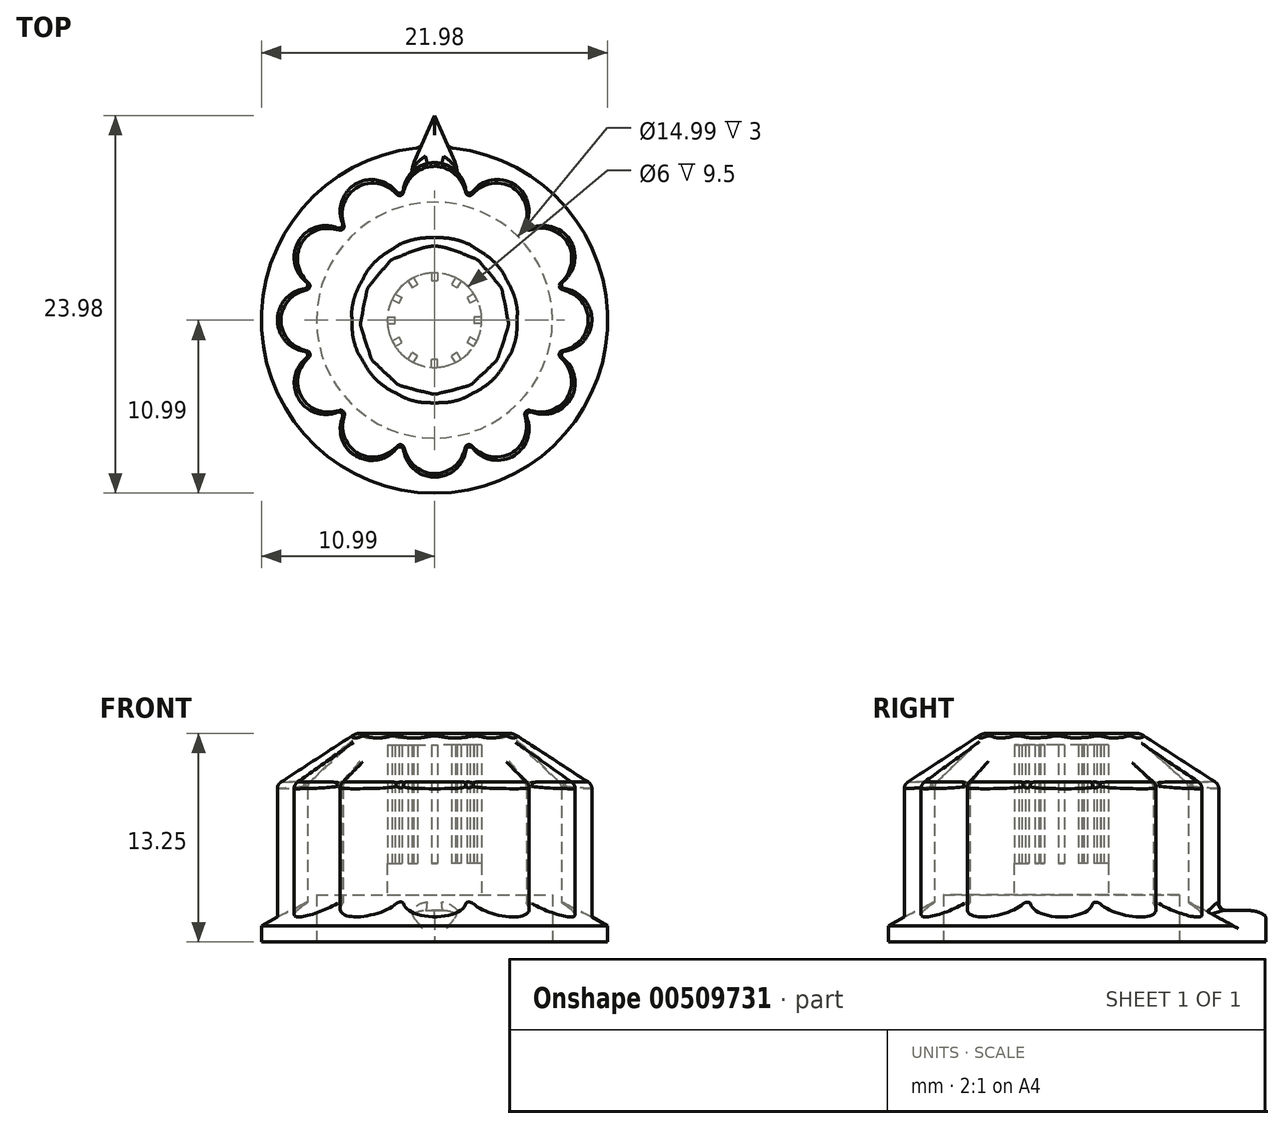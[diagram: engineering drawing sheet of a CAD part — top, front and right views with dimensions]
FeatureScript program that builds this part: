
annotation { "Feature Type Name" : "Feature", "Feature Type Description" : "" }
export const myFeature = defineFeature(function(context is Context, id is Id, definition is map)
    precondition{}
    {
        {
            var Q0;
            Q0=qCreatedBy(makeId("Top.planeOp"),FACE);
            var sketch = newSketch(context, id + "F0", { "sketchPlane" : qUnion([Q0])});
            skArc(sketch, "E0", {"start": v(-1.67, 2.5) * mm, "mid": v(-2.12, 2.12) * mm, "end": v(-2.5, 1.67) * mm});
            skLineSegment(sketch, "E1.top", {"start": v(-0.2, 2.5) * mm, "end": v(0.2, 2.5) * mm});
            skLineSegment(sketch, "E1.left", {"start": v(-0.2, 3) * mm, "end": v(-0.2, 2.5) * mm});
            skLineSegment(sketch, "E1.right", {"start": v(0.2, 3) * mm, "end": v(0.2, 2.5) * mm});
            skLineSegment(sketch, "E2", {"start": v(0, 0) * mm, "end": v(0, 2.5) * mm, "construction": true});
            skLineSegment(sketch, "E3.1.0", {"start": v(-1.32, 2.7) * mm, "end": v(-1.08, 2.27) * mm});
            skLineSegment(sketch, "E3.1.1", {"start": v(-1.42, 2.07) * mm, "end": v(-1.08, 2.27) * mm});
            skLineSegment(sketch, "E3.1.2", {"start": v(-1.67, 2.5) * mm, "end": v(-1.42, 2.07) * mm});
            skLineSegment(sketch, "E3.2.0", {"start": v(-2.5, 1.67) * mm, "end": v(-2.07, 1.42) * mm});
            skLineSegment(sketch, "E3.2.1", {"start": v(-2.27, 1.08) * mm, "end": v(-2.07, 1.42) * mm});
            skLineSegment(sketch, "E3.2.2", {"start": v(-2.7, 1.32) * mm, "end": v(-2.27, 1.08) * mm});
            skLineSegment(sketch, "E3.3.0", {"start": v(-3, 0.2) * mm, "end": v(-2.5, 0.2) * mm});
            skLineSegment(sketch, "E3.3.1", {"start": v(-2.5, -0.2) * mm, "end": v(-2.5, 0.2) * mm});
            skLineSegment(sketch, "E3.3.2", {"start": v(-3, -0.2) * mm, "end": v(-2.5, -0.2) * mm});
            skLineSegment(sketch, "E3.4.0", {"start": v(-2.7, -1.32) * mm, "end": v(-2.27, -1.08) * mm});
            skLineSegment(sketch, "E3.4.1", {"start": v(-2.07, -1.42) * mm, "end": v(-2.27, -1.08) * mm});
            skLineSegment(sketch, "E3.4.2", {"start": v(-2.5, -1.67) * mm, "end": v(-2.07, -1.42) * mm});
            skLineSegment(sketch, "E3.5.0", {"start": v(-1.67, -2.5) * mm, "end": v(-1.42, -2.07) * mm});
            skLineSegment(sketch, "E3.5.1", {"start": v(-1.08, -2.27) * mm, "end": v(-1.42, -2.07) * mm});
            skLineSegment(sketch, "E3.5.2", {"start": v(-1.32, -2.7) * mm, "end": v(-1.08, -2.27) * mm});
            skLineSegment(sketch, "E3.6.0", {"start": v(-0.2, -3) * mm, "end": v(-0.2, -2.5) * mm});
            skLineSegment(sketch, "E3.6.1", {"start": v(0.2, -2.5) * mm, "end": v(-0.2, -2.5) * mm});
            skLineSegment(sketch, "E3.6.2", {"start": v(0.2, -3) * mm, "end": v(0.2, -2.5) * mm});
            skLineSegment(sketch, "E3.7.0", {"start": v(1.32, -2.7) * mm, "end": v(1.08, -2.27) * mm});
            skLineSegment(sketch, "E3.7.1", {"start": v(1.42, -2.07) * mm, "end": v(1.08, -2.27) * mm});
            skLineSegment(sketch, "E3.7.2", {"start": v(1.67, -2.5) * mm, "end": v(1.42, -2.07) * mm});
            skLineSegment(sketch, "E3.8.0", {"start": v(2.5, -1.67) * mm, "end": v(2.07, -1.42) * mm});
            skLineSegment(sketch, "E3.8.1", {"start": v(2.27, -1.08) * mm, "end": v(2.07, -1.42) * mm});
            skLineSegment(sketch, "E3.8.2", {"start": v(2.7, -1.32) * mm, "end": v(2.27, -1.08) * mm});
            skLineSegment(sketch, "E3.9.0", {"start": v(3, -0.2) * mm, "end": v(2.5, -0.2) * mm});
            skLineSegment(sketch, "E3.9.1", {"start": v(2.5, 0.2) * mm, "end": v(2.5, -0.2) * mm});
            skLineSegment(sketch, "E3.9.2", {"start": v(3, 0.2) * mm, "end": v(2.5, 0.2) * mm});
            skLineSegment(sketch, "E3.10.0", {"start": v(2.7, 1.32) * mm, "end": v(2.27, 1.08) * mm});
            skLineSegment(sketch, "E3.10.1", {"start": v(2.07, 1.42) * mm, "end": v(2.27, 1.08) * mm});
            skLineSegment(sketch, "E3.10.2", {"start": v(2.5, 1.67) * mm, "end": v(2.07, 1.42) * mm});
            skLineSegment(sketch, "E3.11.0", {"start": v(1.67, 2.5) * mm, "end": v(1.42, 2.07) * mm});
            skLineSegment(sketch, "E3.11.1", {"start": v(1.08, 2.27) * mm, "end": v(1.42, 2.07) * mm});
            skLineSegment(sketch, "E3.11.2", {"start": v(1.32, 2.7) * mm, "end": v(1.08, 2.27) * mm});
            skArc(sketch, "E4.trimOffspring", {"start": v(-0.2, 3) * mm, "mid": v(-0.78, 2.9) * mm, "end": v(-1.32, 2.7) * mm});
            skArc(sketch, "E5.trimOffspring", {"start": v(1.32, 2.7) * mm, "mid": v(0.78, 2.9) * mm, "end": v(0.2, 3) * mm});
            skArc(sketch, "E6.trimOffspring", {"start": v(2.5, 1.67) * mm, "mid": v(2.12, 2.12) * mm, "end": v(1.67, 2.5) * mm});
            skArc(sketch, "E7.trimOffspring", {"start": v(3, 0.2) * mm, "mid": v(2.9, 0.78) * mm, "end": v(2.7, 1.32) * mm});
            skArc(sketch, "E8.trimOffspring", {"start": v(2.7, -1.32) * mm, "mid": v(2.9, -0.78) * mm, "end": v(3, -0.2) * mm});
            skArc(sketch, "E9.trimOffspring", {"start": v(1.67, -2.5) * mm, "mid": v(2.12, -2.12) * mm, "end": v(2.5, -1.67) * mm});
            skArc(sketch, "E10.trimOffspring", {"start": v(0.2, -3) * mm, "mid": v(0.78, -2.9) * mm, "end": v(1.32, -2.7) * mm});
            skArc(sketch, "E11.trimOffspring", {"start": v(-1.32, -2.7) * mm, "mid": v(-0.78, -2.9) * mm, "end": v(-0.2, -3) * mm});
            skArc(sketch, "E12.trimOffspring", {"start": v(-2.5, -1.67) * mm, "mid": v(-2.12, -2.12) * mm, "end": v(-1.67, -2.5) * mm});
            skArc(sketch, "E13.trimOffspring", {"start": v(-3, -0.2) * mm, "mid": v(-2.9, -0.78) * mm, "end": v(-2.7, -1.32) * mm});
            skArc(sketch, "E14.trimOffspring", {"start": v(-2.7, 1.32) * mm, "mid": v(-2.9, 0.78) * mm, "end": v(-3, 0.2) * mm});
            skCircle(sketch, "E15", {"center": v(0, 0) * mm, "radius": 4 * mm});
            skSolve(sketch);
        }
        {
            var Q0;
            Q0 = qSketchRegion(id + "F0", true);
            extrude(context, id + "F1", {"entities" : qUnion([Q0]), "depth" : 12.25 * mm});
        }
        {
            var Q0;
            Q0=qCreatedBy(makeId("Top.planeOp"),FACE);
            var sketch = newSketch(context, id + "F2", { "sketchPlane" : qUnion([Q0])});
            skCircle(sketch, "E16", {"center": v(0, 0) * mm, "radius": 4 * mm});
            skSolve(sketch);
        }
        {
            var Q0;
            Q0 = qSketchRegion(id + "F2", true);
            extrude(context, id + "F3", {"entities" : qUnion([Q0]), "operationType" : NewBodyOperationType.REMOVE, "depth" : 5 * mm});
        }
        {
            var Q0;
            Q0=makeQuery(id+"F1.opExtrude","CAP_FACE",FACE,{"disambiguationData":[OSD([sQuery(id+"F0.wireOp",EDGE,"E0"),sQuery(id+"F0.wireOp",EDGE,"E1.top"),sQuery(id+"F0.wireOp",EDGE,"E1.left"),sQuery(id+"F0.wireOp",EDGE,"E1.right"),sQuery(id+"F0.wireOp",EDGE,"E3.1.0"),sQuery(id+"F0.wireOp",EDGE,"E3.1.1"),sQuery(id+"F0.wireOp",EDGE,"E3.1.2"),sQuery(id+"F0.wireOp",EDGE,"E3.2.0"),sQuery(id+"F0.wireOp",EDGE,"E3.2.1"),sQuery(id+"F0.wireOp",EDGE,"E3.2.2"),sQuery(id+"F0.wireOp",EDGE,"E3.3.0"),sQuery(id+"F0.wireOp",EDGE,"E3.3.1"),sQuery(id+"F0.wireOp",EDGE,"E3.3.2"),sQuery(id+"F0.wireOp",EDGE,"E3.4.0"),sQuery(id+"F0.wireOp",EDGE,"E3.4.1"),sQuery(id+"F0.wireOp",EDGE,"E3.4.2"),sQuery(id+"F0.wireOp",EDGE,"E3.5.0"),sQuery(id+"F0.wireOp",EDGE,"E3.5.1"),sQuery(id+"F0.wireOp",EDGE,"E3.5.2"),sQuery(id+"F0.wireOp",EDGE,"E3.6.0"),sQuery(id+"F0.wireOp",EDGE,"E3.6.1"),sQuery(id+"F0.wireOp",EDGE,"E3.6.2"),sQuery(id+"F0.wireOp",EDGE,"E3.7.0"),sQuery(id+"F0.wireOp",EDGE,"E3.7.1"),sQuery(id+"F0.wireOp",EDGE,"E3.7.2"),sQuery(id+"F0.wireOp",EDGE,"E3.8.0"),sQuery(id+"F0.wireOp",EDGE,"E3.8.1"),sQuery(id+"F0.wireOp",EDGE,"E3.8.2"),sQuery(id+"F0.wireOp",EDGE,"E3.9.0"),sQuery(id+"F0.wireOp",EDGE,"E3.9.1"),sQuery(id+"F0.wireOp",EDGE,"E3.9.2"),sQuery(id+"F0.wireOp",EDGE,"E3.10.0"),sQuery(id+"F0.wireOp",EDGE,"E3.10.1"),sQuery(id+"F0.wireOp",EDGE,"E3.10.2"),sQuery(id+"F0.wireOp",EDGE,"E3.11.0"),sQuery(id+"F0.wireOp",EDGE,"E3.11.1"),sQuery(id+"F0.wireOp",EDGE,"E3.11.2"),sQuery(id+"F0.wireOp",EDGE,"E4.trimOffspring"),sQuery(id+"F0.wireOp",EDGE,"E5.trimOffspring"),sQuery(id+"F0.wireOp",EDGE,"E6.trimOffspring"),sQuery(id+"F0.wireOp",EDGE,"E7.trimOffspring"),sQuery(id+"F0.wireOp",EDGE,"E8.trimOffspring"),sQuery(id+"F0.wireOp",EDGE,"E9.trimOffspring"),sQuery(id+"F0.wireOp",EDGE,"E10.trimOffspring"),sQuery(id+"F0.wireOp",EDGE,"E11.trimOffspring"),sQuery(id+"F0.wireOp",EDGE,"E12.trimOffspring"),sQuery(id+"F0.wireOp",EDGE,"E13.trimOffspring"),sQuery(id+"F0.wireOp",EDGE,"E14.trimOffspring"),sQuery(id+"F0.wireOp",EDGE,"E15")])],"isStart":false});
            var sketch = newSketch(context, id + "F4", { "sketchPlane" : qUnion([Q0])});
            skCircle(sketch, "E17", {"center": v(0, 0) * mm, "radius": 4 * mm});
            skSolve(sketch);
        }
        {
            var Q0;
            Q0 = qSketchRegion(id + "F4", true);
            extrude(context, id + "F5", {"entities" : qUnion([Q0]), "operationType" : NewBodyOperationType.ADD, "depth" : 1 * mm});
        }
        {
            var Q0;
            Q0=qCreatedBy(makeId("Top.planeOp"),FACE);
            var sketch = newSketch(context, id + "F6", { "sketchPlane" : qUnion([Q0])});
            skLineSegment(sketch, "E18.bottom", {"start": v(0, 10) * mm, "end": v(0, 10) * mm});
            skLineSegment(sketch, "E18.top", {"start": v(-2, 7.5) * mm, "end": v(2, 7.5) * mm, "construction": true});
            skLineSegment(sketch, "E19", {"start": v(0, 7.5) * mm, "end": v(0, 0) * mm, "construction": true});
            skPoint(sketch, "E20.visualSharp", {"position": v(-2, 10) * mm});
            skArc(sketch, "E20.filletArc", {"start": v(0, 10) * mm, "mid": v(-1.3, 9.51) * mm, "end": v(-1.98, 8.29) * mm});
            skPoint(sketch, "E21.visualSharp", {"position": v(2, 10) * mm});
            skArc(sketch, "E21.filletArc", {"start": v(1.98, 8.29) * mm, "mid": v(1.3, 9.51) * mm, "end": v(0, 10) * mm});
            skPoint(sketch, "E22.1.1", {"position": v(-3.26, 9.66) * mm});
            skPoint(sketch, "E22.11.0", {"position": v(3.26, 9.66) * mm});
            skArc(sketch, "E23", {"start": v(1.98, 8.29) * mm, "mid": v(2.04, 8.16) * mm, "end": v(2.16, 8.08) * mm});
            skPoint(sketch, "E24.orphan", {"position": v(2.26, 7.93) * mm});
            skPoint(sketch, "E25.orphan", {"position": v(2, 8) * mm});
            skPoint(sketch, "E26", {"position": v(2.16, 8.08) * mm});
            skArc(sketch, "E27", {"start": v(-2.16, 8.08) * mm, "mid": v(-2.04, 8.15) * mm, "end": v(-1.98, 8.29) * mm});
            skPoint(sketch, "E28.orphan", {"position": v(-2, 8) * mm});
            skPoint(sketch, "E29.orphan", {"position": v(-2.26, 7.93) * mm});
            skPoint(sketch, "E30", {"position": v(-2.16, 8.08) * mm});
            skPoint(sketch, "E31.orphan", {"position": v(-2.01, 7.5) * mm});
            skArc(sketch, "E32.0", {"start": v(-1.95, 7.3) * mm, "mid": v(-1.44, 7.62) * mm, "end": v(-1.19, 8.17) * mm});
            skArc(sketch, "E33.0", {"start": v(1.19, 8.17) * mm, "mid": v(1.44, 7.63) * mm, "end": v(1.96, 7.3) * mm});
            skArc(sketch, "E34", {"start": v(1.19, 8.17) * mm, "mid": v(0, 9.2) * mm, "end": v(-1.19, 8.17) * mm});
            skArc(sketch, "E35.1.2", {"start": v(-2.8, 7.04) * mm, "mid": v(-4.28, 8.1) * mm, "end": v(-5.1, 6.48) * mm});
            skArc(sketch, "E35.1.3", {"start": v(-5, 8.66) * mm, "mid": v(-5.88, 7.58) * mm, "end": v(-5.85, 6.18) * mm});
            skPoint(sketch, "E35.1.4", {"position": v(-5.73, 5.93) * mm});
            skPoint(sketch, "E35.1.5", {"position": v(-5.92, 5.73) * mm});
            skPoint(sketch, "E35.1.6", {"position": v(-6.73, 7.66) * mm});
            skLineSegment(sketch, "E35.1.8", {"start": v(-5, 8.66) * mm, "end": v(-5, 8.66) * mm});
            skPoint(sketch, "E35.1.9", {"position": v(-7.65, 6.73) * mm});
            skLineSegment(sketch, "E35.1.10", {"start": v(-3.74, 6.5) * mm, "end": v(0, 0) * mm, "construction": true});
            skArc(sketch, "E35.1.11", {"start": v(-2.42, 8.17) * mm, "mid": v(-3.62, 8.9) * mm, "end": v(-5, 8.66) * mm});
            skLineSegment(sketch, "E35.1.13", {"start": v(-5.48, 5.5) * mm, "end": v(-2.01, 7.5) * mm, "construction": true});
            skPoint(sketch, "E35.1.14", {"position": v(-5.48, 5.48) * mm});
            skPoint(sketch, "E35.1.15", {"position": v(-5.9, 5.91) * mm});
            skArc(sketch, "E35.1.17", {"start": v(-5.34, 5.35) * mm, "mid": v(-5.05, 5.88) * mm, "end": v(-5.1, 6.48) * mm});
            skArc(sketch, "E35.1.18", {"start": v(-3.05, 7.67) * mm, "mid": v(-2.56, 7.32) * mm, "end": v(-1.95, 7.3) * mm});
            skArc(sketch, "E35.1.19", {"start": v(-5.9, 5.91) * mm, "mid": v(-5.84, 6.04) * mm, "end": v(-5.85, 6.18) * mm});
            skArc(sketch, "E35.1.20", {"start": v(-2.42, 8.17) * mm, "mid": v(-2.3, 8.08) * mm, "end": v(-2.16, 8.08) * mm});
            skPoint(sketch, "E35.2.0", {"position": v(-6.73, 7.66) * mm});
            skPoint(sketch, "E35.2.1", {"position": v(-5.92, 5.73) * mm});
            skArc(sketch, "E35.2.2", {"start": v(-5.94, 4.7) * mm, "mid": v(-7.74, 4.87) * mm, "end": v(-7.66, 3.06) * mm});
            skArc(sketch, "E35.2.3", {"start": v(-8.65, 5) * mm, "mid": v(-8.88, 3.62) * mm, "end": v(-8.15, 2.43) * mm});
            skPoint(sketch, "E35.2.4", {"position": v(-7.92, 2.27) * mm});
            skPoint(sketch, "E35.2.5", {"position": v(-7.98, 2) * mm});
            skPoint(sketch, "E35.2.6", {"position": v(-9.65, 3.27) * mm});
            skPoint(sketch, "E35.2.7", {"position": v(-7.65, 6.73) * mm});
            skLineSegment(sketch, "E35.2.8", {"start": v(-8.65, 5) * mm, "end": v(-8.65, 5) * mm});
            skPoint(sketch, "E35.2.9", {"position": v(-9.98, 2) * mm});
            skLineSegment(sketch, "E35.2.10", {"start": v(-6.48, 3.75) * mm, "end": v(0.01, 0) * mm, "construction": true});
            skArc(sketch, "E35.2.11", {"start": v(-6.18, 5.86) * mm, "mid": v(-7.57, 5.9) * mm, "end": v(-8.65, 5) * mm});
            skPoint(sketch, "E35.2.12", {"position": v(-5.73, 5.93) * mm});
            skLineSegment(sketch, "E35.2.13", {"start": v(-7.48, 2.02) * mm, "end": v(-5.48, 5.48) * mm, "construction": true});
            skPoint(sketch, "E35.2.14", {"position": v(-7.48, 2) * mm});
            skPoint(sketch, "E35.2.15", {"position": v(-8.07, 2.17) * mm});
            skPoint(sketch, "E35.2.16", {"position": v(-5.9, 5.91) * mm});
            skArc(sketch, "E35.2.17", {"start": v(-7.3, 1.96) * mm, "mid": v(-7.31, 2.56) * mm, "end": v(-7.66, 3.06) * mm});
            skArc(sketch, "E35.2.18", {"start": v(-6.47, 5.12) * mm, "mid": v(-5.87, 5.06) * mm, "end": v(-5.34, 5.35) * mm});
            skArc(sketch, "E35.2.19", {"start": v(-8.07, 2.17) * mm, "mid": v(-8.07, 2.31) * mm, "end": v(-8.15, 2.43) * mm});
            skArc(sketch, "E35.2.20", {"start": v(-6.18, 5.86) * mm, "mid": v(-6.03, 5.85) * mm, "end": v(-5.9, 5.91) * mm});
            skPoint(sketch, "E35.3.0", {"position": v(-9.65, 3.27) * mm});
            skPoint(sketch, "E35.3.1", {"position": v(-7.98, 2) * mm});
            skArc(sketch, "E35.3.2", {"start": v(-7.48, 1.1) * mm, "mid": v(-9.13, 0.35) * mm, "end": v(-8.15, -1.18) * mm});
            skArc(sketch, "E35.3.3", {"start": v(-9.98, 0) * mm, "mid": v(-9.5, -1.3) * mm, "end": v(-8.27, -1.97) * mm});
            skPoint(sketch, "E35.3.4", {"position": v(-7.98, -2) * mm});
            skPoint(sketch, "E35.3.5", {"position": v(-7.91, -2.25) * mm});
            skPoint(sketch, "E35.3.6", {"position": v(-9.98, -2) * mm});
            skPoint(sketch, "E35.3.7", {"position": v(-9.98, 2) * mm});
            skLineSegment(sketch, "E35.3.8", {"start": v(-9.98, 0) * mm, "end": v(-9.98, 0) * mm});
            skPoint(sketch, "E35.3.9", {"position": v(-9.64, -3.25) * mm});
            skLineSegment(sketch, "E35.3.10", {"start": v(-7.48, 0) * mm, "end": v(0.02, 0) * mm, "construction": true});
            skArc(sketch, "E35.3.11", {"start": v(-8.27, 1.99) * mm, "mid": v(-9.5, 1.32) * mm, "end": v(-9.98, 0) * mm});
            skPoint(sketch, "E35.3.12", {"position": v(-7.92, 2.27) * mm});
            skLineSegment(sketch, "E35.3.13", {"start": v(-7.48, -2) * mm, "end": v(-7.48, 2) * mm, "construction": true});
            skPoint(sketch, "E35.3.14", {"position": v(-7.48, -2) * mm});
            skPoint(sketch, "E35.3.15", {"position": v(-8.06, -2.16) * mm});
            skPoint(sketch, "E35.3.16", {"position": v(-8.07, 2.17) * mm});
            skArc(sketch, "E35.3.17", {"start": v(-7.3, -1.95) * mm, "mid": v(-7.6, -1.43) * mm, "end": v(-8.15, -1.18) * mm});
            skArc(sketch, "E35.3.18", {"start": v(-8.16, 1.2) * mm, "mid": v(-7.6, 1.45) * mm, "end": v(-7.3, 1.96) * mm});
            skArc(sketch, "E35.3.19", {"start": v(-8.06, -2.16) * mm, "mid": v(-8.14, -2.03) * mm, "end": v(-8.27, -1.97) * mm});
            skArc(sketch, "E35.3.20", {"start": v(-8.27, 1.99) * mm, "mid": v(-8.14, 2.05) * mm, "end": v(-8.07, 2.17) * mm});
            skPoint(sketch, "E35.4.0", {"position": v(-9.98, -2) * mm});
            skPoint(sketch, "E35.4.1", {"position": v(-7.91, -2.25) * mm});
            skArc(sketch, "E35.4.2", {"start": v(-7.02, -2.8) * mm, "mid": v(-8.08, -4.27) * mm, "end": v(-6.47, -5.1) * mm});
            skArc(sketch, "E35.4.3", {"start": v(-8.64, -4.99) * mm, "mid": v(-7.57, -5.88) * mm, "end": v(-6.17, -5.84) * mm});
            skPoint(sketch, "E35.4.4", {"position": v(-5.91, -5.72) * mm});
            skPoint(sketch, "E35.4.5", {"position": v(-5.72, -5.9) * mm});
            skPoint(sketch, "E35.4.6", {"position": v(-7.64, -6.72) * mm});
            skPoint(sketch, "E35.4.7", {"position": v(-9.64, -3.25) * mm});
            skLineSegment(sketch, "E35.4.8", {"start": v(-8.64, -4.99) * mm, "end": v(-8.64, -4.99) * mm});
            skPoint(sketch, "E35.4.9", {"position": v(-6.72, -7.64) * mm});
            skLineSegment(sketch, "E35.4.10", {"start": v(-6.48, -3.74) * mm, "end": v(0.02, 0.01) * mm, "construction": true});
            skArc(sketch, "E35.4.11", {"start": v(-8.15, -2.42) * mm, "mid": v(-8.87, -3.6) * mm, "end": v(-8.64, -4.99) * mm});
            skPoint(sketch, "E35.4.12", {"position": v(-7.98, -2) * mm});
            skLineSegment(sketch, "E35.4.13", {"start": v(-5.48, -5.47) * mm, "end": v(-7.48, -2) * mm, "construction": true});
            skPoint(sketch, "E35.4.14", {"position": v(-5.47, -5.48) * mm});
            skPoint(sketch, "E35.4.15", {"position": v(-5.9, -5.9) * mm});
            skPoint(sketch, "E35.4.16", {"position": v(-8.06, -2.16) * mm});
            skArc(sketch, "E35.4.17", {"start": v(-5.33, -5.33) * mm, "mid": v(-5.86, -5.05) * mm, "end": v(-6.47, -5.1) * mm});
            skArc(sketch, "E35.4.18", {"start": v(-7.65, -3.04) * mm, "mid": v(-7.3, -2.55) * mm, "end": v(-7.3, -1.95) * mm});
            skArc(sketch, "E35.4.19", {"start": v(-5.9, -5.9) * mm, "mid": v(-6.02, -5.83) * mm, "end": v(-6.17, -5.84) * mm});
            skArc(sketch, "E35.4.20", {"start": v(-8.15, -2.42) * mm, "mid": v(-8.07, -2.3) * mm, "end": v(-8.06, -2.16) * mm});
            skPoint(sketch, "E35.5.0", {"position": v(-7.64, -6.72) * mm});
            skPoint(sketch, "E35.5.1", {"position": v(-5.72, -5.9) * mm});
            skArc(sketch, "E35.5.2", {"start": v(-4.68, -5.93) * mm, "mid": v(-4.85, -7.74) * mm, "end": v(-3.04, -7.65) * mm});
            skArc(sketch, "E35.5.3", {"start": v(-4.98, -8.64) * mm, "mid": v(-3.6, -8.87) * mm, "end": v(-2.41, -8.15) * mm});
            skPoint(sketch, "E35.5.4", {"position": v(-2.25, -7.9) * mm});
            skPoint(sketch, "E35.5.5", {"position": v(-2, -7.98) * mm});
            skPoint(sketch, "E35.5.6", {"position": v(-3.25, -9.64) * mm});
            skPoint(sketch, "E35.5.7", {"position": v(-6.72, -7.64) * mm});
            skLineSegment(sketch, "E35.5.8", {"start": v(-4.98, -8.64) * mm, "end": v(-4.98, -8.64) * mm});
            skPoint(sketch, "E35.5.9", {"position": v(-2, -9.98) * mm});
            skLineSegment(sketch, "E35.5.10", {"start": v(-3.73, -6.48) * mm, "end": v(0.02, 0.02) * mm, "construction": true});
            skArc(sketch, "E35.5.11", {"start": v(-5.84, -6.17) * mm, "mid": v(-5.87, -7.56) * mm, "end": v(-4.98, -8.64) * mm});
            skPoint(sketch, "E35.5.12", {"position": v(-5.91, -5.72) * mm});
            skLineSegment(sketch, "E35.5.13", {"start": v(-2, -7.48) * mm, "end": v(-5.47, -5.48) * mm, "construction": true});
            skPoint(sketch, "E35.5.14", {"position": v(-2, -7.48) * mm});
            skPoint(sketch, "E35.5.15", {"position": v(-2.15, -8.06) * mm});
            skPoint(sketch, "E35.5.16", {"position": v(-5.9, -5.9) * mm});
            skArc(sketch, "E35.5.17", {"start": v(-1.95, -7.29) * mm, "mid": v(-2.55, -7.3) * mm, "end": v(-3.04, -7.65) * mm});
            skArc(sketch, "E35.5.18", {"start": v(-5.1, -6.46) * mm, "mid": v(-5.05, -5.86) * mm, "end": v(-5.33, -5.33) * mm});
            skArc(sketch, "E35.5.19", {"start": v(-2.15, -8.06) * mm, "mid": v(-2.3, -8.06) * mm, "end": v(-2.41, -8.15) * mm});
            skArc(sketch, "E35.5.20", {"start": v(-5.84, -6.17) * mm, "mid": v(-5.83, -6.03) * mm, "end": v(-5.9, -5.9) * mm});
            skPoint(sketch, "E35.6.0", {"position": v(-3.25, -9.64) * mm});
            skPoint(sketch, "E35.6.1", {"position": v(-2, -7.98) * mm});
            skArc(sketch, "E35.6.2", {"start": v(-1.08, -7.48) * mm, "mid": v(-0.33, -9.13) * mm, "end": v(1.2, -8.15) * mm});
            skArc(sketch, "E35.6.3", {"start": v(0, -9.98) * mm, "mid": v(1.32, -9.49) * mm, "end": v(1.99, -8.26) * mm});
            skPoint(sketch, "E35.6.4", {"position": v(2, -7.98) * mm});
            skPoint(sketch, "E35.6.5", {"position": v(2.27, -7.9) * mm});
            skPoint(sketch, "E35.6.6", {"position": v(2, -9.98) * mm});
            skPoint(sketch, "E35.6.7", {"position": v(-2, -9.98) * mm});
            skLineSegment(sketch, "E35.6.8", {"start": v(0, -9.98) * mm, "end": v(0, -9.98) * mm});
            skPoint(sketch, "E35.6.9", {"position": v(3.27, -9.64) * mm});
            skLineSegment(sketch, "E35.6.10", {"start": v(0, -7.48) * mm, "end": v(0, 0.02) * mm, "construction": true});
            skArc(sketch, "E35.6.11", {"start": v(-1.97, -8.26) * mm, "mid": v(-1.3, -9.49) * mm, "end": v(0, -9.98) * mm});
            skPoint(sketch, "E35.6.12", {"position": v(-2.25, -7.9) * mm});
            skLineSegment(sketch, "E35.6.13", {"start": v(2, -7.48) * mm, "end": v(-2, -7.48) * mm, "construction": true});
            skPoint(sketch, "E35.6.14", {"position": v(2.02, -7.47) * mm});
            skPoint(sketch, "E35.6.15", {"position": v(2.17, -8.06) * mm});
            skPoint(sketch, "E35.6.16", {"position": v(-2.15, -8.06) * mm});
            skArc(sketch, "E35.6.17", {"start": v(1.96, -7.28) * mm, "mid": v(1.45, -7.6) * mm, "end": v(1.2, -8.15) * mm});
            skArc(sketch, "E35.6.18", {"start": v(-1.18, -8.15) * mm, "mid": v(-1.43, -7.6) * mm, "end": v(-1.95, -7.29) * mm});
            skArc(sketch, "E35.6.19", {"start": v(2.17, -8.06) * mm, "mid": v(2.05, -8.13) * mm, "end": v(1.99, -8.26) * mm});
            skArc(sketch, "E35.6.20", {"start": v(-1.97, -8.26) * mm, "mid": v(-2.03, -8.13) * mm, "end": v(-2.15, -8.06) * mm});
            skPoint(sketch, "E35.7.0", {"position": v(2, -9.98) * mm});
            skPoint(sketch, "E35.7.1", {"position": v(2.27, -7.9) * mm});
            skArc(sketch, "E35.7.2", {"start": v(2.8, -7.02) * mm, "mid": v(4.29, -8.07) * mm, "end": v(5.12, -6.46) * mm});
            skArc(sketch, "E35.7.3", {"start": v(5, -8.64) * mm, "mid": v(5.9, -7.56) * mm, "end": v(5.86, -6.16) * mm});
            skPoint(sketch, "E35.7.4", {"position": v(5.74, -5.9) * mm});
            skPoint(sketch, "E35.7.5", {"position": v(5.93, -5.71) * mm});
            skPoint(sketch, "E35.7.6", {"position": v(6.74, -7.64) * mm});
            skPoint(sketch, "E35.7.7", {"position": v(3.27, -9.64) * mm});
            skLineSegment(sketch, "E35.7.8", {"start": v(5, -8.64) * mm, "end": v(5, -8.64) * mm});
            skPoint(sketch, "E35.7.9", {"position": v(7.66, -6.71) * mm});
            skLineSegment(sketch, "E35.7.10", {"start": v(3.75, -6.47) * mm, "end": v(0, 0.02) * mm, "construction": true});
            skArc(sketch, "E35.7.11", {"start": v(2.43, -8.14) * mm, "mid": v(3.63, -8.87) * mm, "end": v(5, -8.64) * mm});
            skPoint(sketch, "E35.7.12", {"position": v(2, -7.98) * mm});
            skLineSegment(sketch, "E35.7.13", {"start": v(5.49, -5.47) * mm, "end": v(2.02, -7.47) * mm, "construction": true});
            skPoint(sketch, "E35.7.14", {"position": v(5.5, -5.46) * mm});
            skPoint(sketch, "E35.7.15", {"position": v(5.92, -5.9) * mm});
            skPoint(sketch, "E35.7.16", {"position": v(2.17, -8.06) * mm});
            skArc(sketch, "E35.7.17", {"start": v(5.35, -5.33) * mm, "mid": v(5.06, -5.86) * mm, "end": v(5.12, -6.46) * mm});
            skArc(sketch, "E35.7.18", {"start": v(3.06, -7.65) * mm, "mid": v(2.57, -7.3) * mm, "end": v(1.96, -7.28) * mm});
            skArc(sketch, "E35.7.19", {"start": v(5.92, -5.9) * mm, "mid": v(5.85, -6.02) * mm, "end": v(5.86, -6.16) * mm});
            skArc(sketch, "E35.7.20", {"start": v(2.43, -8.14) * mm, "mid": v(2.32, -8.06) * mm, "end": v(2.17, -8.06) * mm});
            skPoint(sketch, "E35.8.0", {"position": v(6.74, -7.64) * mm});
            skPoint(sketch, "E35.8.1", {"position": v(5.93, -5.71) * mm});
            skArc(sketch, "E35.8.2", {"start": v(5.95, -4.67) * mm, "mid": v(7.75, -4.85) * mm, "end": v(7.67, -3.04) * mm});
            skArc(sketch, "E35.8.3", {"start": v(8.66, -4.98) * mm, "mid": v(8.89, -3.6) * mm, "end": v(8.16, -2.4) * mm});
            skPoint(sketch, "E35.8.4", {"position": v(7.93, -2.25) * mm});
            skPoint(sketch, "E35.8.5", {"position": v(8, -1.98) * mm});
            skPoint(sketch, "E35.8.6", {"position": v(9.66, -3.25) * mm});
            skPoint(sketch, "E35.8.7", {"position": v(7.66, -6.71) * mm});
            skLineSegment(sketch, "E35.8.8", {"start": v(8.66, -4.98) * mm, "end": v(8.66, -4.98) * mm});
            skPoint(sketch, "E35.8.9", {"position": v(10, -1.98) * mm});
            skLineSegment(sketch, "E35.8.10", {"start": v(6.5, -3.73) * mm, "end": v(0, 0.02) * mm, "construction": true});
            skArc(sketch, "E35.8.11", {"start": v(6.19, -5.84) * mm, "mid": v(7.58, -5.87) * mm, "end": v(8.66, -4.98) * mm});
            skPoint(sketch, "E35.8.12", {"position": v(5.74, -5.9) * mm});
            skLineSegment(sketch, "E35.8.13", {"start": v(7.5, -2) * mm, "end": v(5.5, -5.46) * mm, "construction": true});
            skPoint(sketch, "E35.8.14", {"position": v(7.5, -1.98) * mm});
            skPoint(sketch, "E35.8.15", {"position": v(8.08, -2.15) * mm});
            skPoint(sketch, "E35.8.16", {"position": v(5.92, -5.9) * mm});
            skArc(sketch, "E35.8.17", {"start": v(7.3, -1.94) * mm, "mid": v(7.32, -2.54) * mm, "end": v(7.67, -3.04) * mm});
            skArc(sketch, "E35.8.18", {"start": v(6.48, -5.1) * mm, "mid": v(5.88, -5.04) * mm, "end": v(5.35, -5.33) * mm});
            skArc(sketch, "E35.8.19", {"start": v(8.08, -2.15) * mm, "mid": v(8.08, -2.29) * mm, "end": v(8.16, -2.4) * mm});
            skArc(sketch, "E35.8.20", {"start": v(6.19, -5.84) * mm, "mid": v(6.04, -5.82) * mm, "end": v(5.92, -5.9) * mm});
            skPoint(sketch, "E35.9.0", {"position": v(9.66, -3.25) * mm});
            skPoint(sketch, "E35.9.1", {"position": v(8, -1.98) * mm});
            skArc(sketch, "E35.9.2", {"start": v(7.5, -1.07) * mm, "mid": v(9.14, -0.32) * mm, "end": v(8.16, 1.2) * mm});
            skArc(sketch, "E35.9.3", {"start": v(10, 0.02) * mm, "mid": v(9.5, 1.33) * mm, "end": v(8.28, 2) * mm});
            skPoint(sketch, "E35.9.4", {"position": v(8, 2.02) * mm});
            skPoint(sketch, "E35.9.5", {"position": v(7.92, 2.28) * mm});
            skPoint(sketch, "E35.9.6", {"position": v(10, 2.02) * mm});
            skPoint(sketch, "E35.9.7", {"position": v(10, -1.98) * mm});
            skLineSegment(sketch, "E35.9.8", {"start": v(10, 0.02) * mm, "end": v(10, 0.02) * mm});
            skPoint(sketch, "E35.9.9", {"position": v(9.65, 3.28) * mm});
            skLineSegment(sketch, "E35.9.10", {"start": v(7.5, 0.02) * mm, "end": v(0, 0.02) * mm, "construction": true});
            skArc(sketch, "E35.9.11", {"start": v(8.28, -1.96) * mm, "mid": v(9.5, -1.3) * mm, "end": v(10, 0.02) * mm});
            skPoint(sketch, "E35.9.12", {"position": v(7.93, -2.25) * mm});
            skLineSegment(sketch, "E35.9.13", {"start": v(7.5, 2.02) * mm, "end": v(7.5, -1.98) * mm, "construction": true});
            skPoint(sketch, "E35.9.14", {"position": v(7.49, 2.03) * mm});
            skPoint(sketch, "E35.9.15", {"position": v(8.07, 2.18) * mm});
            skPoint(sketch, "E35.9.16", {"position": v(8.08, -2.15) * mm});
            skArc(sketch, "E35.9.17", {"start": v(7.3, 1.97) * mm, "mid": v(7.62, 1.46) * mm, "end": v(8.16, 1.2) * mm});
            skArc(sketch, "E35.9.18", {"start": v(8.17, -1.17) * mm, "mid": v(7.62, -1.43) * mm, "end": v(7.3, -1.94) * mm});
            skArc(sketch, "E35.9.19", {"start": v(8.07, 2.18) * mm, "mid": v(8.15, 2.06) * mm, "end": v(8.28, 2) * mm});
            skArc(sketch, "E35.9.20", {"start": v(8.28, -1.96) * mm, "mid": v(8.15, -2.02) * mm, "end": v(8.08, -2.15) * mm});
            skPoint(sketch, "E35.10.0", {"position": v(10, 2.02) * mm});
            skPoint(sketch, "E35.10.1", {"position": v(7.92, 2.28) * mm});
            skArc(sketch, "E35.10.2", {"start": v(7.03, 2.82) * mm, "mid": v(8.09, 4.3) * mm, "end": v(6.47, 5.12) * mm});
            skArc(sketch, "E35.10.3", {"start": v(8.65, 5.01) * mm, "mid": v(7.58, 5.9) * mm, "end": v(6.18, 5.87) * mm});
            skPoint(sketch, "E35.10.4", {"position": v(5.92, 5.74) * mm});
            skPoint(sketch, "E35.10.5", {"position": v(5.73, 5.93) * mm});
            skPoint(sketch, "E35.10.6", {"position": v(7.65, 6.74) * mm});
            skPoint(sketch, "E35.10.7", {"position": v(9.65, 3.28) * mm});
            skLineSegment(sketch, "E35.10.8", {"start": v(8.65, 5.01) * mm, "end": v(8.65, 5.01) * mm});
            skPoint(sketch, "E35.10.9", {"position": v(6.73, 7.66) * mm});
            skLineSegment(sketch, "E35.10.10", {"start": v(6.49, 3.76) * mm, "end": v(0, 0.01) * mm, "construction": true});
            skArc(sketch, "E35.10.11", {"start": v(8.16, 2.44) * mm, "mid": v(8.88, 3.63) * mm, "end": v(8.65, 5.01) * mm});
            skPoint(sketch, "E35.10.12", {"position": v(8, 2.02) * mm});
            skLineSegment(sketch, "E35.10.13", {"start": v(5.49, 5.5) * mm, "end": v(7.49, 2.03) * mm, "construction": true});
            skPoint(sketch, "E35.10.14", {"position": v(5.48, 5.5) * mm});
            skPoint(sketch, "E35.10.15", {"position": v(5.9, 5.92) * mm});
            skPoint(sketch, "E35.10.16", {"position": v(8.07, 2.18) * mm});
            skArc(sketch, "E35.10.17", {"start": v(5.34, 5.36) * mm, "mid": v(5.87, 5.07) * mm, "end": v(6.47, 5.12) * mm});
            skArc(sketch, "E35.10.18", {"start": v(7.66, 3.07) * mm, "mid": v(7.32, 2.57) * mm, "end": v(7.3, 1.97) * mm});
            skArc(sketch, "E35.10.19", {"start": v(5.9, 5.92) * mm, "mid": v(6.03, 5.85) * mm, "end": v(6.18, 5.87) * mm});
            skArc(sketch, "E35.10.20", {"start": v(8.16, 2.44) * mm, "mid": v(8.08, 2.32) * mm, "end": v(8.07, 2.18) * mm});
            skPoint(sketch, "E35.11.0", {"position": v(7.65, 6.74) * mm});
            skPoint(sketch, "E35.11.1", {"position": v(5.73, 5.93) * mm});
            skArc(sketch, "E35.11.2", {"start": v(4.69, 5.95) * mm, "mid": v(4.86, 7.76) * mm, "end": v(3.05, 7.67) * mm});
            skArc(sketch, "E35.11.3", {"start": v(5, 8.66) * mm, "mid": v(3.62, 8.9) * mm, "end": v(2.42, 8.17) * mm});
            skPoint(sketch, "E35.11.7", {"position": v(6.73, 7.66) * mm});
            skLineSegment(sketch, "E35.11.8", {"start": v(5, 8.66) * mm, "end": v(5, 8.66) * mm});
            skLineSegment(sketch, "E35.11.10", {"start": v(3.74, 6.5) * mm, "end": v(0, 0) * mm, "construction": true});
            skArc(sketch, "E35.11.11", {"start": v(5.85, 6.2) * mm, "mid": v(5.88, 7.59) * mm, "end": v(5, 8.66) * mm});
            skPoint(sketch, "E35.11.12", {"position": v(5.92, 5.74) * mm});
            skLineSegment(sketch, "E35.11.13", {"start": v(2.01, 7.5) * mm, "end": v(5.48, 5.5) * mm, "construction": true});
            skPoint(sketch, "E35.11.14", {"position": v(2, 7.5) * mm});
            skPoint(sketch, "E35.11.16", {"position": v(5.9, 5.92) * mm});
            skArc(sketch, "E35.11.17", {"start": v(1.96, 7.3) * mm, "mid": v(2.56, 7.33) * mm, "end": v(3.05, 7.67) * mm});
            skArc(sketch, "E35.11.18", {"start": v(5.1, 6.49) * mm, "mid": v(5.06, 5.89) * mm, "end": v(5.34, 5.36) * mm});
            skArc(sketch, "E35.11.19", {"start": v(2.16, 8.08) * mm, "mid": v(2.3, 8.09) * mm, "end": v(2.42, 8.17) * mm});
            skArc(sketch, "E35.11.20", {"start": v(5.85, 6.2) * mm, "mid": v(5.84, 6.05) * mm, "end": v(5.9, 5.92) * mm});
            skPoint(sketch, "E35.center", {"position": v(0, 0.01) * mm});
            skPoint(sketch, "E36.orphan", {"position": v(1.1, 7.5) * mm});
            skSolve(sketch);
        }
        {
            var Q0;
            Q0 = qSketchRegion(id + "F6", true);
            extrude(context, id + "F7", {"entities" : qUnion([Q0]), "depth" : 10 * mm});
        }
        {
            var Q0;
            Q0=makeQuery(id+"F5.opExtrude","CAP_FACE",FACE,{"disambiguationData":[OSD([sQuery(id+"F4.wireOp",EDGE,"E17")])],"isStart":false});
            var sketch = newSketch(context, id + "F8", { "sketchPlane" : qUnion([Q0])});
            skCircle(sketch, "E37", {"center": v(0, 0) * mm, "radius": 5 * mm});
            skPoint(sketch, "E38", {"position": v(0, 5) * mm});
            skSolve(sketch);
        }
        {
            var Q0;
            Q0=makeQuery(id+"F7.opExtrude","CAP_FACE",FACE,{"disambiguationData":[OSD([sQuery(id+"F6.wireOp",EDGE,"E20.filletArc"),sQuery(id+"F6.wireOp",EDGE,"E21.filletArc"),sQuery(id+"F6.wireOp",EDGE,"E23"),sQuery(id+"F6.wireOp",EDGE,"E27"),sQuery(id+"F6.wireOp",EDGE,"E32.0"),sQuery(id+"F6.wireOp",EDGE,"E33.0"),sQuery(id+"F6.wireOp",EDGE,"E34"),sQuery(id+"F6.wireOp",EDGE,"E35.1.2"),sQuery(id+"F6.wireOp",EDGE,"E35.1.3"),sQuery(id+"F6.wireOp",EDGE,"E35.1.11"),sQuery(id+"F6.wireOp",EDGE,"E35.1.17"),sQuery(id+"F6.wireOp",EDGE,"E35.1.18"),sQuery(id+"F6.wireOp",EDGE,"E35.1.19"),sQuery(id+"F6.wireOp",EDGE,"E35.1.20"),sQuery(id+"F6.wireOp",EDGE,"E35.2.2"),sQuery(id+"F6.wireOp",EDGE,"E35.2.3"),sQuery(id+"F6.wireOp",EDGE,"E35.2.11"),sQuery(id+"F6.wireOp",EDGE,"E35.2.17"),sQuery(id+"F6.wireOp",EDGE,"E35.2.18"),sQuery(id+"F6.wireOp",EDGE,"E35.2.19"),sQuery(id+"F6.wireOp",EDGE,"E35.2.20"),sQuery(id+"F6.wireOp",EDGE,"E35.3.2"),sQuery(id+"F6.wireOp",EDGE,"E35.3.3"),sQuery(id+"F6.wireOp",EDGE,"E35.3.11"),sQuery(id+"F6.wireOp",EDGE,"E35.3.17"),sQuery(id+"F6.wireOp",EDGE,"E35.3.18"),sQuery(id+"F6.wireOp",EDGE,"E35.3.19"),sQuery(id+"F6.wireOp",EDGE,"E35.3.20"),sQuery(id+"F6.wireOp",EDGE,"E35.4.2"),sQuery(id+"F6.wireOp",EDGE,"E35.4.3"),sQuery(id+"F6.wireOp",EDGE,"E35.4.11"),sQuery(id+"F6.wireOp",EDGE,"E35.4.17"),sQuery(id+"F6.wireOp",EDGE,"E35.4.18"),sQuery(id+"F6.wireOp",EDGE,"E35.4.19"),sQuery(id+"F6.wireOp",EDGE,"E35.4.20"),sQuery(id+"F6.wireOp",EDGE,"E35.5.2"),sQuery(id+"F6.wireOp",EDGE,"E35.5.3"),sQuery(id+"F6.wireOp",EDGE,"E35.5.11"),sQuery(id+"F6.wireOp",EDGE,"E35.5.17"),sQuery(id+"F6.wireOp",EDGE,"E35.5.18"),sQuery(id+"F6.wireOp",EDGE,"E35.5.19"),sQuery(id+"F6.wireOp",EDGE,"E35.5.20"),sQuery(id+"F6.wireOp",EDGE,"E35.6.2"),sQuery(id+"F6.wireOp",EDGE,"E35.6.3"),sQuery(id+"F6.wireOp",EDGE,"E35.6.11"),sQuery(id+"F6.wireOp",EDGE,"E35.6.17"),sQuery(id+"F6.wireOp",EDGE,"E35.6.18"),sQuery(id+"F6.wireOp",EDGE,"E35.6.19"),sQuery(id+"F6.wireOp",EDGE,"E35.6.20"),sQuery(id+"F6.wireOp",EDGE,"E35.7.2"),sQuery(id+"F6.wireOp",EDGE,"E35.7.3"),sQuery(id+"F6.wireOp",EDGE,"E35.7.11"),sQuery(id+"F6.wireOp",EDGE,"E35.7.17"),sQuery(id+"F6.wireOp",EDGE,"E35.7.18"),sQuery(id+"F6.wireOp",EDGE,"E35.7.19"),sQuery(id+"F6.wireOp",EDGE,"E35.7.20"),sQuery(id+"F6.wireOp",EDGE,"E35.8.2"),sQuery(id+"F6.wireOp",EDGE,"E35.8.3"),sQuery(id+"F6.wireOp",EDGE,"E35.8.11"),sQuery(id+"F6.wireOp",EDGE,"E35.8.17"),sQuery(id+"F6.wireOp",EDGE,"E35.8.18"),sQuery(id+"F6.wireOp",EDGE,"E35.8.19"),sQuery(id+"F6.wireOp",EDGE,"E35.8.20"),sQuery(id+"F6.wireOp",EDGE,"E35.9.2"),sQuery(id+"F6.wireOp",EDGE,"E35.9.3"),sQuery(id+"F6.wireOp",EDGE,"E35.9.11"),sQuery(id+"F6.wireOp",EDGE,"E35.9.17"),sQuery(id+"F6.wireOp",EDGE,"E35.9.18"),sQuery(id+"F6.wireOp",EDGE,"E35.9.19"),sQuery(id+"F6.wireOp",EDGE,"E35.9.20"),sQuery(id+"F6.wireOp",EDGE,"E35.10.2"),sQuery(id+"F6.wireOp",EDGE,"E35.10.3"),sQuery(id+"F6.wireOp",EDGE,"E35.10.11"),sQuery(id+"F6.wireOp",EDGE,"E35.10.17"),sQuery(id+"F6.wireOp",EDGE,"E35.10.18"),sQuery(id+"F6.wireOp",EDGE,"E35.10.19"),sQuery(id+"F6.wireOp",EDGE,"E35.10.20"),sQuery(id+"F6.wireOp",EDGE,"E35.11.2"),sQuery(id+"F6.wireOp",EDGE,"E35.11.3"),sQuery(id+"F6.wireOp",EDGE,"E35.11.11"),sQuery(id+"F6.wireOp",EDGE,"E35.11.17"),sQuery(id+"F6.wireOp",EDGE,"E35.11.18"),sQuery(id+"F6.wireOp",EDGE,"E35.11.19"),sQuery(id+"F6.wireOp",EDGE,"E35.11.20")])],"isStart":false});
            var sketch = newSketch(context, id + "F9", { "sketchPlane" : qUnion([Q0])});
            skArc(sketch, "E39.0.0", {"start": v(-2.41, -8.15) * mm, "mid": v(-2.15, -8.06) * mm, "end": v(-1.97, -8.26) * mm});
            skArc(sketch, "E39.0.1", {"start": v(-1.97, -8.26) * mm, "mid": v(0.01, -9.98) * mm, "end": v(1.99, -8.26) * mm});
            skArc(sketch, "E39.0.2", {"start": v(1.99, -8.26) * mm, "mid": v(2.17, -8.06) * mm, "end": v(2.43, -8.14) * mm});
            skArc(sketch, "E39.0.3", {"start": v(2.43, -8.14) * mm, "mid": v(5, -8.64) * mm, "end": v(5.86, -6.16) * mm});
            skArc(sketch, "E39.0.4", {"start": v(5.86, -6.16) * mm, "mid": v(5.92, -5.9) * mm, "end": v(6.19, -5.84) * mm});
            skArc(sketch, "E39.0.5", {"start": v(6.19, -5.84) * mm, "mid": v(8.66, -4.98) * mm, "end": v(8.16, -2.4) * mm});
            skArc(sketch, "E39.0.6", {"start": v(8.16, -2.4) * mm, "mid": v(8.08, -2.15) * mm, "end": v(8.28, -1.96) * mm});
            skArc(sketch, "E39.0.7", {"start": v(8.28, -1.96) * mm, "mid": v(10, 0.02) * mm, "end": v(8.28, 2) * mm});
            skArc(sketch, "E39.0.8", {"start": v(8.28, 2) * mm, "mid": v(8.07, 2.18) * mm, "end": v(8.16, 2.44) * mm});
            skArc(sketch, "E39.0.9", {"start": v(8.16, 2.44) * mm, "mid": v(8.65, 5.01) * mm, "end": v(6.18, 5.87) * mm});
            skArc(sketch, "E39.0.10", {"start": v(6.18, 5.87) * mm, "mid": v(5.9, 5.92) * mm, "end": v(5.85, 6.2) * mm});
            skArc(sketch, "E39.0.11", {"start": v(5.85, 6.2) * mm, "mid": v(5, 8.66) * mm, "end": v(2.42, 8.17) * mm});
            skArc(sketch, "E39.0.12", {"start": v(2.42, 8.17) * mm, "mid": v(2.16, 8.08) * mm, "end": v(1.98, 8.29) * mm});
            skArc(sketch, "E39.0.13", {"start": v(1.98, 8.29) * mm, "mid": v(0, 10) * mm, "end": v(-1.98, 8.29) * mm});
            skArc(sketch, "E39.0.14", {"start": v(-1.98, 8.29) * mm, "mid": v(-2.16, 8.08) * mm, "end": v(-2.42, 8.17) * mm});
            skArc(sketch, "E39.0.15", {"start": v(-2.42, 8.17) * mm, "mid": v(-5, 8.66) * mm, "end": v(-5.85, 6.18) * mm});
            skArc(sketch, "E39.0.16", {"start": v(-5.85, 6.18) * mm, "mid": v(-5.9, 5.91) * mm, "end": v(-6.18, 5.86) * mm});
            skArc(sketch, "E39.0.17", {"start": v(-6.18, 5.86) * mm, "mid": v(-8.65, 5) * mm, "end": v(-8.15, 2.43) * mm});
            skArc(sketch, "E39.0.18", {"start": v(-8.15, 2.43) * mm, "mid": v(-8.07, 2.17) * mm, "end": v(-8.27, 1.99) * mm});
            skArc(sketch, "E39.0.19", {"start": v(-8.27, 1.99) * mm, "mid": v(-9.98, 0) * mm, "end": v(-8.27, -1.97) * mm});
            skArc(sketch, "E39.0.20", {"start": v(-8.27, -1.97) * mm, "mid": v(-8.06, -2.16) * mm, "end": v(-8.15, -2.42) * mm});
            skArc(sketch, "E39.0.21", {"start": v(-8.15, -2.42) * mm, "mid": v(-8.64, -4.99) * mm, "end": v(-6.17, -5.84) * mm});
            skArc(sketch, "E39.0.22", {"start": v(-6.17, -5.84) * mm, "mid": v(-5.9, -5.9) * mm, "end": v(-5.84, -6.17) * mm});
            skArc(sketch, "E39.0.23", {"start": v(-5.84, -6.17) * mm, "mid": v(-4.98, -8.64) * mm, "end": v(-2.41, -8.15) * mm});
            skPoint(sketch, "E40", {"position": v(0, 10) * mm});
            skSolve(sketch);
        }
        {
            var Q0;
            Q0=qCreatedBy(makeId("Top.planeOp"),FACE);
            var sketch = newSketch(context, id + "F10", { "sketchPlane" : qUnion([Q0])});
            skArc(sketch, "E41.0", {"start": v(5.12, -6.46) * mm, "mid": v(4.6, -7.94) * mm, "end": v(3.06, -7.65) * mm});
            skArc(sketch, "E42.0", {"start": v(5.12, -6.46) * mm, "mid": v(5.35, -5.33) * mm, "end": v(6.48, -5.1) * mm});
            skArc(sketch, "E43.0", {"start": v(7.67, -3.04) * mm, "mid": v(7.97, -4.58) * mm, "end": v(6.48, -5.1) * mm});
            skArc(sketch, "E44.0", {"start": v(7.67, -3.04) * mm, "mid": v(7.3, -1.94) * mm, "end": v(8.17, -1.17) * mm});
            skArc(sketch, "E45.0", {"start": v(8.16, 1.2) * mm, "mid": v(9.2, 0.02) * mm, "end": v(8.17, -1.17) * mm});
            skArc(sketch, "E46.0", {"start": v(8.16, 1.2) * mm, "mid": v(7.3, 1.97) * mm, "end": v(7.66, 3.07) * mm});
            skArc(sketch, "E47.0", {"start": v(6.47, 5.12) * mm, "mid": v(7.96, 4.61) * mm, "end": v(7.66, 3.07) * mm});
            skArc(sketch, "E48.0", {"start": v(6.47, 5.12) * mm, "mid": v(5.34, 5.36) * mm, "end": v(5.1, 6.49) * mm});
            skArc(sketch, "E49.0", {"start": v(3.05, 7.67) * mm, "mid": v(4.6, 7.97) * mm, "end": v(5.1, 6.49) * mm});
            skPoint(sketch, "E50.0", {"position": v(1.96, 7.3) * mm});
            skArc(sketch, "E51.0", {"start": v(3.05, 7.67) * mm, "mid": v(1.96, 7.3) * mm, "end": v(1.19, 8.17) * mm});
            skArc(sketch, "E52.0", {"start": v(-1.19, 8.17) * mm, "mid": v(0, 9.2) * mm, "end": v(1.19, 8.17) * mm});
            skArc(sketch, "E53.0", {"start": v(-1.19, 8.17) * mm, "mid": v(-1.95, 7.3) * mm, "end": v(-3.05, 7.67) * mm});
            skArc(sketch, "E54.0", {"start": v(-5.1, 6.48) * mm, "mid": v(-4.6, 7.97) * mm, "end": v(-3.05, 7.67) * mm});
            skArc(sketch, "E55.0", {"start": v(-5.1, 6.48) * mm, "mid": v(-5.34, 5.35) * mm, "end": v(-6.47, 5.12) * mm});
            skArc(sketch, "E56.0", {"start": v(-7.66, 3.06) * mm, "mid": v(-7.96, 4.6) * mm, "end": v(-6.47, 5.12) * mm});
            skArc(sketch, "E57.0", {"start": v(-7.66, 3.06) * mm, "mid": v(-7.3, 1.96) * mm, "end": v(-8.16, 1.2) * mm});
            skArc(sketch, "E58.0", {"start": v(-8.15, -1.18) * mm, "mid": v(-9.18, 0) * mm, "end": v(-8.16, 1.2) * mm});
            skArc(sketch, "E59.0", {"start": v(-8.15, -1.18) * mm, "mid": v(-7.3, -1.95) * mm, "end": v(-7.65, -3.04) * mm});
            skArc(sketch, "E60.0", {"start": v(-6.47, -5.1) * mm, "mid": v(-7.95, -4.59) * mm, "end": v(-7.65, -3.04) * mm});
            skArc(sketch, "E61.0", {"start": v(-6.47, -5.1) * mm, "mid": v(-5.33, -5.33) * mm, "end": v(-5.1, -6.46) * mm});
            skArc(sketch, "E62.0", {"start": v(-3.04, -7.65) * mm, "mid": v(-4.58, -7.95) * mm, "end": v(-5.1, -6.46) * mm});
            skArc(sketch, "E63.0", {"start": v(-3.04, -7.65) * mm, "mid": v(-1.95, -7.29) * mm, "end": v(-1.18, -8.15) * mm});
            skArc(sketch, "E64.0", {"start": v(1.2, -8.15) * mm, "mid": v(0.01, -9.18) * mm, "end": v(-1.18, -8.15) * mm});
            skPoint(sketch, "E65.0", {"position": v(1.96, -7.28) * mm});
            skArc(sketch, "E66.0", {"start": v(1.2, -8.15) * mm, "mid": v(1.96, -7.28) * mm, "end": v(3.06, -7.65) * mm});
            skCircle(sketch, "E67", {"center": v(0, 0) * mm, "radius": 3 * mm});
            skSolve(sketch);
        }
        {
            var Q0;
            Q0 = qSketchRegion(id + "F10", true);
            extrude(context, id + "F11", {"entities" : qUnion([Q0]), "operationType" : NewBodyOperationType.ADD, "depth" : 10 * mm});
        }
        {
            var Q1;
            Q1 = qSketchRegion(id + "F9", true);
            var Q2;
            Q2 = qSketchRegion(id + "F8", true);
            var Q3;
            Q3=sQuery(id+"F9.wireOp",VERTEX,"E40");
            var Q4;
            Q4=sQuery(id+"F8.wireOp",VERTEX,"E38");
            loft(context, id + "F12", {"operationType" : NewBodyOperationType.ADD, "sheetProfilesArray" : [{ "sheetProfileEntities" : qUnion([Q1]) }, { "sheetProfileEntities" : qUnion([Q2]) }], "matchConnections" : true, "connections" : [{ "connectionEntities" : qUnion([Q3, Q4]), "connectionEdgeQueries" : qUnion([]), "connectionEdgeParameters" : [] }]});
        }
        {
            var Q0;
            Q0=makeQuery(id+"F12.opLoft","MID_CAP_EDGE",EDGE,{"disambiguationData":[OSD([sQuery(id+"F9.wireOp",EDGE,"E39.0.16"),sQuery(id+"F9.wireOp",EDGE,"E39.0.17"),sQuery(id+"F9.wireOp",EDGE,"E39.0.18")])],"capPos":0.0});
            fillet(context, id + "F13", {"entities" : qUnion([Q0]), "radius" : 0.5 * mm, "tangentPropagation" : true, "allowEdgeOverflow" : false});
        }
        {
            var Q0;
            Q0=makeQuery(id+"F12.opLoft","MID_CAP_EDGE",EDGE,{"disambiguationData":[OSD([sQuery(id+"F8.wireOp",EDGE,"E37"),sQuery(id+"F9.wireOp",EDGE,"E39.0.17"),sQuery(id+"F9.wireOp",EDGE,"E39.0.18"),sQuery(id+"F9.wireOp",EDGE,"E39.0.19")])],"capPos":1.0});
            fillet(context, id + "F14", {"entities" : qUnion([Q0]), "radius" : 1 * mm, "tangentPropagation" : true, "allowEdgeOverflow" : false});
        }
        {
            var Q0;
            Q0=qCreatedBy(makeId("Right.planeOp"),FACE);
            var sketch = newSketch(context, id + "F15", { "sketchPlane" : qUnion([Q0])});
            skLineSegment(sketch, "E68", {"start": v(-11, 0) * mm, "end": v(-3, 0) * mm});
            skLineSegment(sketch, "E69", {"start": v(-3, 0) * mm, "end": v(-3, 5.62) * mm});
            skLineSegment(sketch, "E70", {"start": v(-3, 5.62) * mm, "end": v(-11, 1) * mm});
            skLineSegment(sketch, "E71", {"start": v(-11, 1) * mm, "end": v(-11, 0) * mm});
            skLineSegment(sketch, "E72", {"start": v(0, 0) * mm, "end": v(0, 1.42) * mm, "construction": true});
            skSolve(sketch);
        }
        {
            var Q0;
            Q0=makeQuery(id+"F15.imprint","IMPRINT",FACE,{"disambiguationData":[TD([[makeQuery(id+"F15.imprint","IMPRINT",EDGE,{"derivedFrom":sQuery(id+"F15.wireOp",EDGE,"E68")}),1.0]])]});
            var Q1;
            Q1=sQuery(id+"F15.wireOp",EDGE,"E72");
            revolve(context, id + "F16", {"operationType" : NewBodyOperationType.ADD, "entities" : qUnion([Q0]), "axis" : qUnion([Q1]), "revolveType" : RevolveType.FULL});
        }
        {
            var Q0;
            Q0 = qSketchRegion(id + "F0", true);
            extrude(context, id + "F17", {"entities" : qUnion([Q0]), "operationType" : NewBodyOperationType.REMOVE, "oppositeDirection" : true, "depth" : 25 * mm});
        }
        {
            var Q0;
            Q0=makeQuery(id+"F0.imprint","IMPRINT",FACE,{"disambiguationData":[TD([[makeQuery(id+"F0.imprint","IMPRINT",EDGE,{"derivedFrom":sQuery(id+"F0.wireOp",EDGE,"E0")}),1.0]])]});
            extrude(context, id + "F18", {"entities" : qUnion([Q0]), "operationType" : NewBodyOperationType.REMOVE, "depth" : 12.5 * mm});
        }
        {
            var Q0;
            Q0=makeQuery(id+"F16.boolean.opBoolean","MERGE",FACE,{"derivedFrom":[makeQuery(id+"F12.boolean.opBoolean","MERGE",FACE,{"derivedFrom":[makeQuery(id+"F7.opExtrude","CAP_FACE",FACE,{"disambiguationData":[OSD([sQuery(id+"F6.wireOp",EDGE,"E20.filletArc"),sQuery(id+"F6.wireOp",EDGE,"E21.filletArc"),sQuery(id+"F6.wireOp",EDGE,"E23"),sQuery(id+"F6.wireOp",EDGE,"E27"),sQuery(id+"F6.wireOp",EDGE,"E32.0"),sQuery(id+"F6.wireOp",EDGE,"E33.0"),sQuery(id+"F6.wireOp",EDGE,"E34"),sQuery(id+"F6.wireOp",EDGE,"E35.1.2"),sQuery(id+"F6.wireOp",EDGE,"E35.1.3"),sQuery(id+"F6.wireOp",EDGE,"E35.1.11"),sQuery(id+"F6.wireOp",EDGE,"E35.1.17"),sQuery(id+"F6.wireOp",EDGE,"E35.1.18"),sQuery(id+"F6.wireOp",EDGE,"E35.1.19"),sQuery(id+"F6.wireOp",EDGE,"E35.1.20"),sQuery(id+"F6.wireOp",EDGE,"E35.2.2"),sQuery(id+"F6.wireOp",EDGE,"E35.2.3"),sQuery(id+"F6.wireOp",EDGE,"E35.2.11"),sQuery(id+"F6.wireOp",EDGE,"E35.2.17"),sQuery(id+"F6.wireOp",EDGE,"E35.2.18"),sQuery(id+"F6.wireOp",EDGE,"E35.2.19"),sQuery(id+"F6.wireOp",EDGE,"E35.2.20"),sQuery(id+"F6.wireOp",EDGE,"E35.3.2"),sQuery(id+"F6.wireOp",EDGE,"E35.3.3"),sQuery(id+"F6.wireOp",EDGE,"E35.3.11"),sQuery(id+"F6.wireOp",EDGE,"E35.3.17"),sQuery(id+"F6.wireOp",EDGE,"E35.3.18"),sQuery(id+"F6.wireOp",EDGE,"E35.3.19"),sQuery(id+"F6.wireOp",EDGE,"E35.3.20"),sQuery(id+"F6.wireOp",EDGE,"E35.4.2"),sQuery(id+"F6.wireOp",EDGE,"E35.4.3"),sQuery(id+"F6.wireOp",EDGE,"E35.4.11"),sQuery(id+"F6.wireOp",EDGE,"E35.4.17"),sQuery(id+"F6.wireOp",EDGE,"E35.4.18"),sQuery(id+"F6.wireOp",EDGE,"E35.4.19"),sQuery(id+"F6.wireOp",EDGE,"E35.4.20"),sQuery(id+"F6.wireOp",EDGE,"E35.5.2"),sQuery(id+"F6.wireOp",EDGE,"E35.5.3"),sQuery(id+"F6.wireOp",EDGE,"E35.5.11"),sQuery(id+"F6.wireOp",EDGE,"E35.5.17"),sQuery(id+"F6.wireOp",EDGE,"E35.5.18"),sQuery(id+"F6.wireOp",EDGE,"E35.5.19"),sQuery(id+"F6.wireOp",EDGE,"E35.5.20"),sQuery(id+"F6.wireOp",EDGE,"E35.6.2"),sQuery(id+"F6.wireOp",EDGE,"E35.6.3"),sQuery(id+"F6.wireOp",EDGE,"E35.6.11"),sQuery(id+"F6.wireOp",EDGE,"E35.6.17"),sQuery(id+"F6.wireOp",EDGE,"E35.6.18"),sQuery(id+"F6.wireOp",EDGE,"E35.6.19"),sQuery(id+"F6.wireOp",EDGE,"E35.6.20"),sQuery(id+"F6.wireOp",EDGE,"E35.7.2"),sQuery(id+"F6.wireOp",EDGE,"E35.7.3"),sQuery(id+"F6.wireOp",EDGE,"E35.7.11"),sQuery(id+"F6.wireOp",EDGE,"E35.7.17"),sQuery(id+"F6.wireOp",EDGE,"E35.7.18"),sQuery(id+"F6.wireOp",EDGE,"E35.7.19"),sQuery(id+"F6.wireOp",EDGE,"E35.7.20"),sQuery(id+"F6.wireOp",EDGE,"E35.8.2"),sQuery(id+"F6.wireOp",EDGE,"E35.8.3"),sQuery(id+"F6.wireOp",EDGE,"E35.8.11"),sQuery(id+"F6.wireOp",EDGE,"E35.8.17"),sQuery(id+"F6.wireOp",EDGE,"E35.8.18"),sQuery(id+"F6.wireOp",EDGE,"E35.8.19"),sQuery(id+"F6.wireOp",EDGE,"E35.8.20"),sQuery(id+"F6.wireOp",EDGE,"E35.9.2"),sQuery(id+"F6.wireOp",EDGE,"E35.9.3"),sQuery(id+"F6.wireOp",EDGE,"E35.9.11"),sQuery(id+"F6.wireOp",EDGE,"E35.9.17"),sQuery(id+"F6.wireOp",EDGE,"E35.9.18"),sQuery(id+"F6.wireOp",EDGE,"E35.9.19"),sQuery(id+"F6.wireOp",EDGE,"E35.9.20"),sQuery(id+"F6.wireOp",EDGE,"E35.10.2"),sQuery(id+"F6.wireOp",EDGE,"E35.10.3"),sQuery(id+"F6.wireOp",EDGE,"E35.10.11"),sQuery(id+"F6.wireOp",EDGE,"E35.10.17"),sQuery(id+"F6.wireOp",EDGE,"E35.10.18"),sQuery(id+"F6.wireOp",EDGE,"E35.10.19"),sQuery(id+"F6.wireOp",EDGE,"E35.10.20"),sQuery(id+"F6.wireOp",EDGE,"E35.11.2"),sQuery(id+"F6.wireOp",EDGE,"E35.11.3"),sQuery(id+"F6.wireOp",EDGE,"E35.11.11"),sQuery(id+"F6.wireOp",EDGE,"E35.11.17"),sQuery(id+"F6.wireOp",EDGE,"E35.11.18"),sQuery(id+"F6.wireOp",EDGE,"E35.11.19"),sQuery(id+"F6.wireOp",EDGE,"E35.11.20")])],"isStart":true}),makeQuery(id+"F11.opExtrude","CAP_FACE",FACE,{"disambiguationData":[OSD([sQuery(id+"F10.wireOp",EDGE,"E41.0"),sQuery(id+"F10.wireOp",EDGE,"E42.0"),sQuery(id+"F10.wireOp",EDGE,"E43.0"),sQuery(id+"F10.wireOp",EDGE,"E44.0"),sQuery(id+"F10.wireOp",EDGE,"E45.0"),sQuery(id+"F10.wireOp",EDGE,"E46.0"),sQuery(id+"F10.wireOp",EDGE,"E47.0"),sQuery(id+"F10.wireOp",EDGE,"E48.0"),sQuery(id+"F10.wireOp",EDGE,"E49.0"),sQuery(id+"F10.wireOp",EDGE,"E51.0"),sQuery(id+"F10.wireOp",EDGE,"E52.0"),sQuery(id+"F10.wireOp",EDGE,"E53.0"),sQuery(id+"F10.wireOp",EDGE,"E54.0"),sQuery(id+"F10.wireOp",EDGE,"E55.0"),sQuery(id+"F10.wireOp",EDGE,"E56.0"),sQuery(id+"F10.wireOp",EDGE,"E57.0"),sQuery(id+"F10.wireOp",EDGE,"E58.0"),sQuery(id+"F10.wireOp",EDGE,"E59.0"),sQuery(id+"F10.wireOp",EDGE,"E60.0"),sQuery(id+"F10.wireOp",EDGE,"E61.0"),sQuery(id+"F10.wireOp",EDGE,"E62.0"),sQuery(id+"F10.wireOp",EDGE,"E63.0"),sQuery(id+"F10.wireOp",EDGE,"E64.0"),sQuery(id+"F10.wireOp",EDGE,"E66.0"),sQuery(id+"F10.wireOp",EDGE,"E67")])],"isStart":true})]}),makeQuery(id+"F16.opRevolve","SWEPT_FACE",FACE,{"disambiguationData":[OSD([sQuery(id+"F15.wireOp",EDGE,"E68")])]})]});
            var sketch = newSketch(context, id + "F19", { "sketchPlane" : qUnion([Q0])});
            skCircle(sketch, "E73", {"center": v(0, 0) * mm, "radius": 7.5 * mm});
            skSolve(sketch);
        }
        {
            var Q0;
            Q0 = qSketchRegion(id + "F19", true);
            extrude(context, id + "F20", {"entities" : qUnion([Q0]), "operationType" : NewBodyOperationType.REMOVE, "oppositeDirection" : true, "depth" : 3 * mm});
        }
        {
            var Q0;
            Q0=qCreatedBy(makeId("Top.planeOp"),FACE);
            var sketch = newSketch(context, id + "F21", { "sketchPlane" : qUnion([Q0])});
            skLineSegment(sketch, "E74", {"start": v(-1.83, 8.8) * mm, "end": v(0, 13) * mm});
            skLineSegment(sketch, "E75", {"start": v(0, 13) * mm, "end": v(1.83, 8.8) * mm});
            skLineSegment(sketch, "E76", {"start": v(1.83, 8.8) * mm, "end": v(-1.83, 8.8) * mm});
            skSolve(sketch);
        }
        {
            var Q0;
            Q0 = qSketchRegion(id + "F21", true);
            extrude(context, id + "F22", {"entities" : qUnion([Q0]), "operationType" : NewBodyOperationType.ADD, "depth" : 2 * mm});
        }
        {
            var Q0;
            Q0=makeQuery(id+"F22.opExtrude","CAP_EDGE",EDGE,{"disambiguationData":[OSD([sQuery(id+"F21.wireOp",EDGE,"E75")])],"isStart":false});
            var Q1;
            Q1=makeQuery(id+"F22.opExtrude","CAP_EDGE",EDGE,{"disambiguationData":[OSD([sQuery(id+"F21.wireOp",EDGE,"E74")])],"isStart":false});
            var Q2;
            Q2=makeQuery(id+"F22.boolean.opBoolean","INTERSECT",EDGE,{"derivedFrom":[makeQuery(id+"F16.opRevolve","SWEPT_FACE",FACE,{"disambiguationData":[OSD([sQuery(id+"F15.wireOp",EDGE,"E71")])]}),makeQuery(id+"F22.opExtrude","SWEPT_FACE",FACE,{"disambiguationData":[OSD([sQuery(id+"F21.wireOp",EDGE,"E75")])]})]});
            var Q3;
            Q3=makeQuery(id+"F22.boolean.opBoolean","INTERSECT",EDGE,{"derivedFrom":[makeQuery(id+"F16.opRevolve","SWEPT_FACE",FACE,{"disambiguationData":[OSD([sQuery(id+"F15.wireOp",EDGE,"E71")])]}),makeQuery(id+"F22.opExtrude","SWEPT_FACE",FACE,{"disambiguationData":[OSD([sQuery(id+"F21.wireOp",EDGE,"E74")])]})]});
            fillet(context, id + "F23", {"entities" : qUnion([Q0, Q1, Q2, Q3]), "radius" : 0.5 * mm, "tangentPropagation" : true, "allowEdgeOverflow" : false});
        }
        {
            var Q0;
            Q0=makeQuery(id+"F22.boolean.opBoolean","INTERSECT",EDGE,{"derivedFrom":[makeQuery(id+"F7.opExtrude","SWEPT_FACE",FACE,{"disambiguationData":[OSD([sQuery(id+"F6.wireOp",EDGE,"E20.filletArc"),sQuery(id+"F6.wireOp",EDGE,"E21.filletArc")])]}),makeQuery(id+"F22.opExtrude","CAP_FACE",FACE,{"disambiguationData":[OSD([sQuery(id+"F21.wireOp",EDGE,"E74"),sQuery(id+"F21.wireOp",EDGE,"E75"),sQuery(id+"F21.wireOp",EDGE,"E76")])],"isStart":false})]});
            fillet(context, id + "F24", {"entities" : qUnion([Q0]), "radius" : 0.5 * mm, "tangentPropagation" : true, "allowEdgeOverflow" : false});
        }
    });
